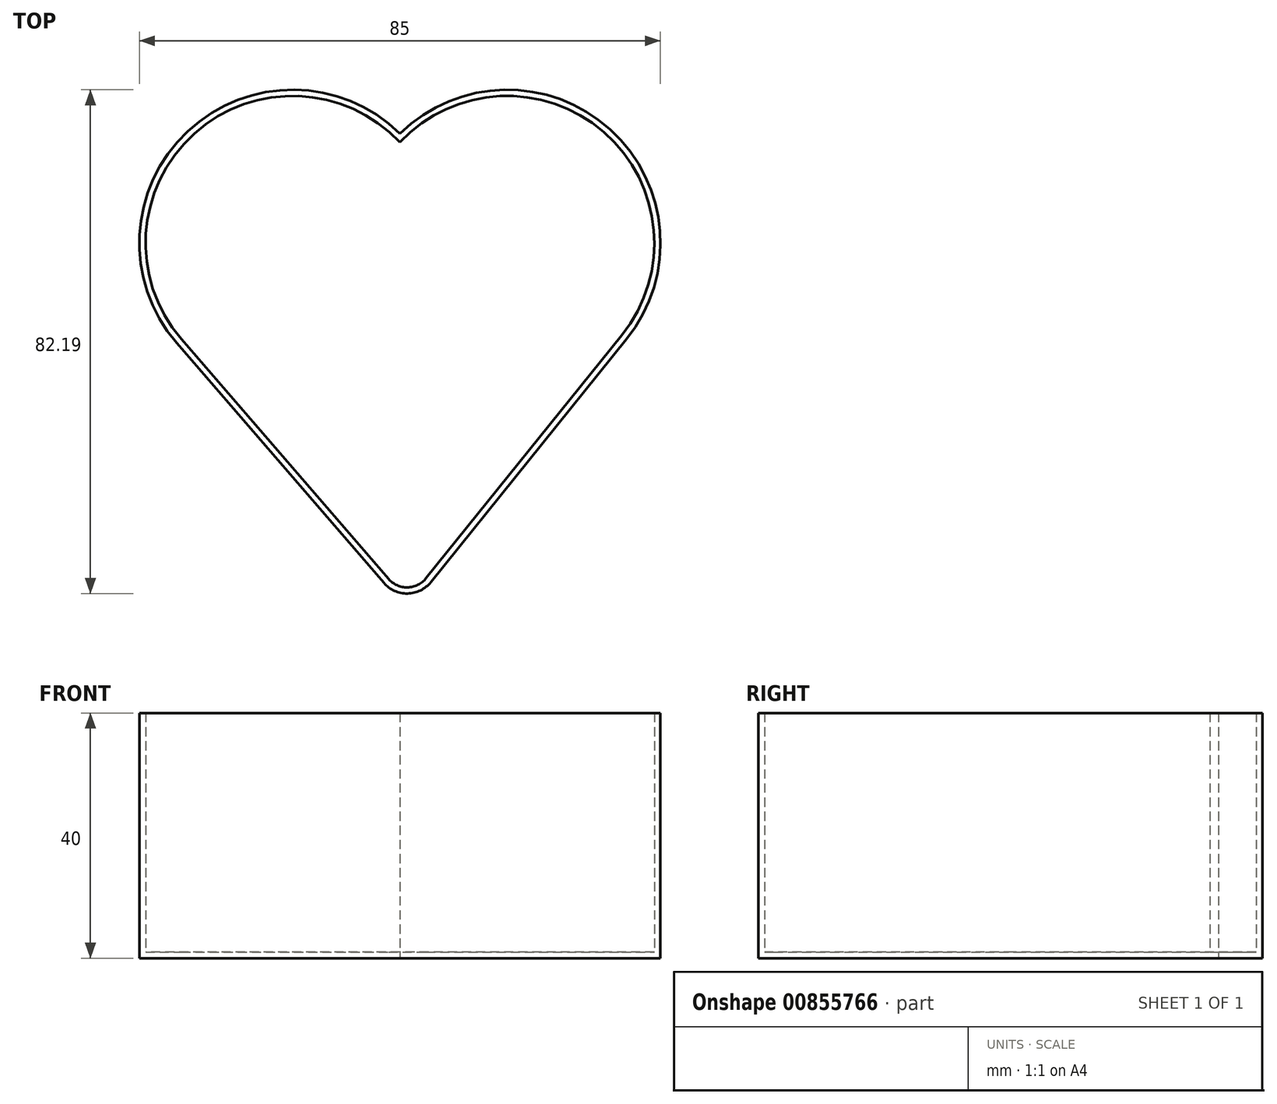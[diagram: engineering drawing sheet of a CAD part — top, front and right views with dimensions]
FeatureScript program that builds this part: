
annotation { "Feature Type Name" : "Feature", "Feature Type Description" : "" }
export const myFeature = defineFeature(function(context is Context, id is Id, definition is map)
    precondition{}
    {
        {
            var Q0;
            Q0=qCreatedBy(makeId("Top.planeOp"),FACE);
            var sketch = newSketch(context, id + "F0", { "sketchPlane" : qUnion([Q0])});
            skCircle(sketch, "E0", {"center": v(-18.79, 0) * mm, "radius": 25 * mm});
            skCircle(sketch, "E1", {"center": v(16.21, 0) * mm, "radius": 25 * mm});
            skLineSegment(sketch, "E2", {"start": v(-37.7, -16.34) * mm, "end": v(0, -60) * mm});
            skLineSegment(sketch, "E3", {"start": v(0, -60) * mm, "end": v(35.69, -15.68) * mm});
            skSolve(sketch);
        }
        {
            var Q0;
            Q0 = qSketchRegion(id + "F0", true);
            extrude(context, id + "F1", {"entities" : qUnion([Q0]), "depth" : 40 * mm, "offsetDistance" : 25 * mm});
        }
        {
            var Q0;
            Q0=makeQuery(id+"F1.opExtrude","SWEPT_EDGE",EDGE,{"disambiguationData":[OSD([sQuery(id+"F0.wireOp",EDGE,"E2"),sQuery(id+"F0.wireOp",EDGE,"E3")])]});
            fillet(context, id + "F2", {"entities" : qUnion([Q0]), "radius" : 5 * mm, "tangentPropagation" : true, "allowEdgeOverflow" : false});
        }
        {
            var Q0;
            Q0=makeQuery(id+"F1.opExtrude","CAP_FACE",FACE,{"disambiguationData":[OSD([sQuery(id+"F0.wireOp",EDGE,"E0"),sQuery(id+"F0.wireOp",EDGE,"E1"),sQuery(id+"F0.wireOp",EDGE,"E2"),sQuery(id+"F0.wireOp",EDGE,"E3")])],"isStart":false});
            shell(context, id + "F3", {"entities" : qUnion([Q0]), "thickness" : 1 * mm});
        }
    });
